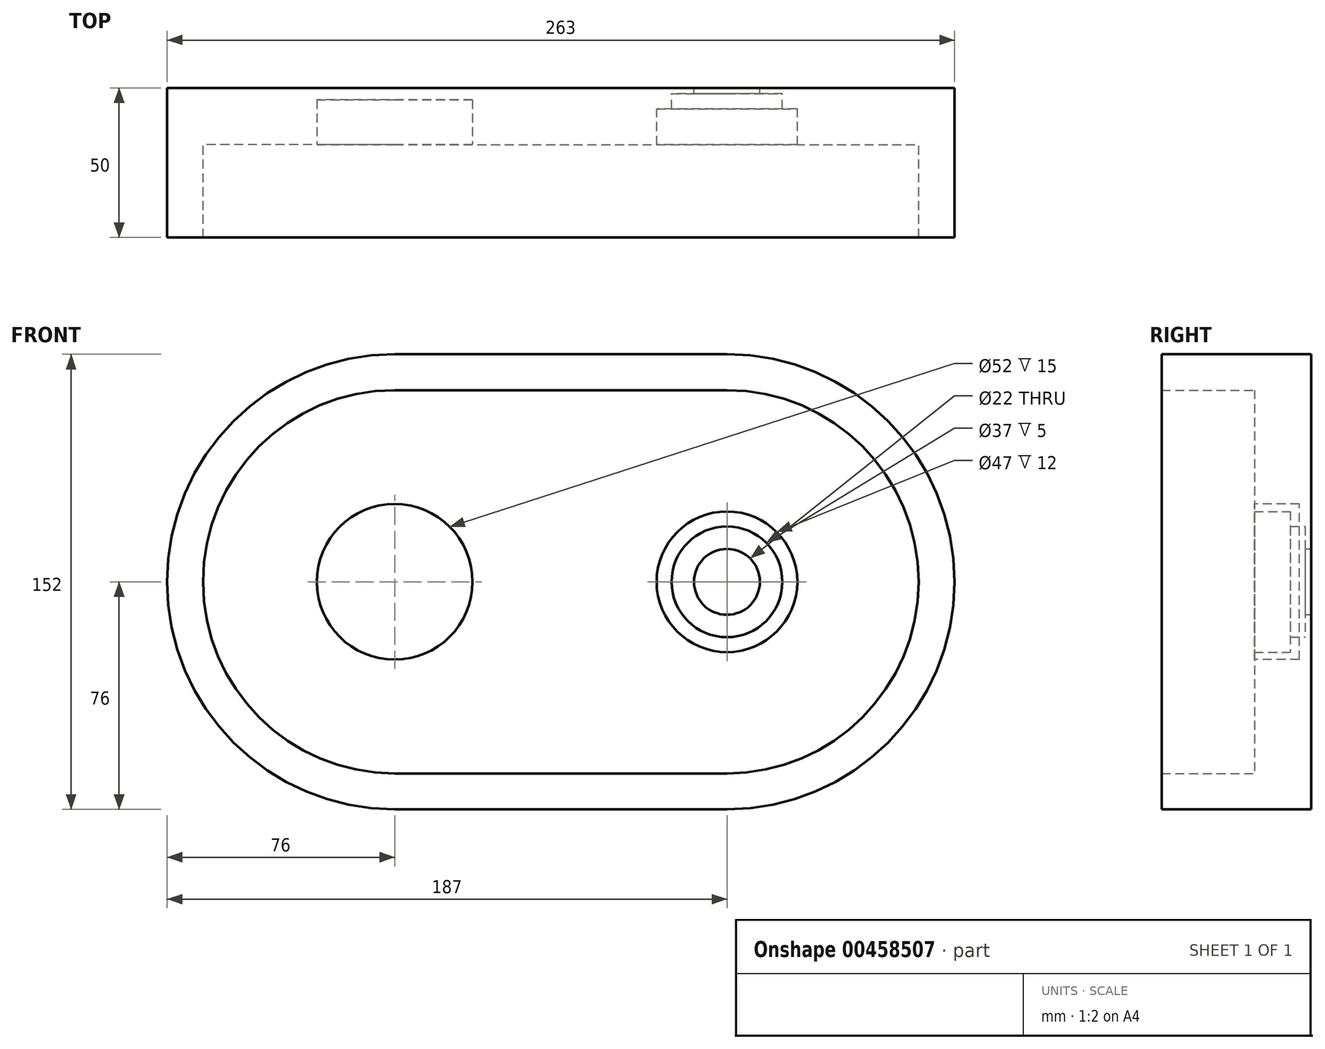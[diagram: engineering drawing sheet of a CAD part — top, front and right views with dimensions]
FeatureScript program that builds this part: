
annotation { "Feature Type Name" : "Feature", "Feature Type Description" : "" }
export const myFeature = defineFeature(function(context is Context, id is Id, definition is map)
    precondition{}
    {
        {
            var Q0;
            Q0=qCreatedBy(makeId("Front.planeOp"),FACE);
            var sketch = newSketch(context, id + "F0", { "sketchPlane" : qUnion([Q0])});
            skArc(sketch, "E0", {"start": v(0, 76) * mm, "mid": v(-76, 0) * mm, "end": v(0, -76) * mm});
            skArc(sketch, "E1", {"start": v(111, -76) * mm, "mid": v(187, 0) * mm, "end": v(111, 76) * mm});
            skLineSegment(sketch, "E2", {"start": v(0, 76) * mm, "end": v(111, 76) * mm});
            skLineSegment(sketch, "E3", {"start": v(111, -76) * mm, "end": v(0, -76) * mm});
            skSolve(sketch);
        }
        {
            var Q0;
            Q0=makeQuery(id+"F0.imprint","IMPRINT",FACE,{"disambiguationData":[TD([[makeQuery(id+"F0.imprint","IMPRINT",EDGE,{"derivedFrom":sQuery(id+"F0.wireOp",EDGE,"E0")}),1.0]])]});
            extrude(context, id + "F1", {"entities" : qUnion([Q0]), "depth" : 50 * mm, "offsetDistance" : 25 * mm});
        }
        {
            var Q0;
            Q0=qCreatedBy(makeId("Front.planeOp"),FACE);
            cPlane(context, id + "F2", {"entities" : qUnion([Q0]), "cplaneType" : CPlaneType.OFFSET, "offset" : 19 * mm, "width" : 150 * mm, "height" : 150 * mm});
        }
        {
            var Q0;
            Q0=qCreatedBy(id+"F2.planeOp",FACE);
            var sketch = newSketch(context, id + "F3", { "sketchPlane" : qUnion([Q0])});
            skArc(sketch, "E4", {"start": v(0, 64) * mm, "mid": v(-64, 0) * mm, "end": v(0, -64) * mm});
            skArc(sketch, "E5", {"start": v(111, -64) * mm, "mid": v(175, 0) * mm, "end": v(111, 64) * mm});
            skLineSegment(sketch, "E6", {"start": v(0, 64) * mm, "end": v(111, 64) * mm});
            skLineSegment(sketch, "E7", {"start": v(0, -64) * mm, "end": v(111, -64) * mm});
            skCircle(sketch, "E8", {"center": v(0, 0) * mm, "radius": 26 * mm});
            skSolve(sketch);
        }
        {
            var Q0;
            Q0 = qSketchRegion(id + "F3", true);
            extrude(context, id + "F4", {"entities" : qUnion([Q0]), "operationType" : NewBodyOperationType.REMOVE, "depth" : 50 * mm, "offsetDistance" : 25 * mm});
        }
        {
            var Q0;
            Q0=makeQuery(id+"F4.boolean.opBoolean","SPLIT",FACE,{"disambiguationData":[TD([makeQuery(id+"F4.opExtrude","SWEPT_FACE",FACE,{"disambiguationData":[OSD([sQuery(id+"F3.wireOp",EDGE,"E8")])]})])],"derivedFrom":makeQuery(id+"F1.opExtrude","CAP_FACE",FACE,{"disambiguationData":[OSD([sQuery(id+"F0.wireOp",EDGE,"E0"),sQuery(id+"F0.wireOp",EDGE,"E1"),sQuery(id+"F0.wireOp",EDGE,"E2"),sQuery(id+"F0.wireOp",EDGE,"E3")])],"isStart":false})});
            extrude(context, id + "F5", {"entities" : qUnion([Q0]), "operationType" : NewBodyOperationType.REMOVE, "oppositeDirection" : true, "depth" : 46 * mm, "offsetDistance" : 25 * mm});
        }
        {
            var Q0;
            Q0=qCreatedBy(makeId("Right.planeOp"),FACE);
            cPlane(context, id + "F6", {"entities" : qUnion([Q0]), "cplaneType" : CPlaneType.OFFSET, "offset" : 111 * mm, "width" : 150 * mm, "height" : 150 * mm});
        }
        {
            var Q0;
            Q0=qCreatedBy(id+"F6.planeOp",FACE);
            var sketch = newSketch(context, id + "F7", { "sketchPlane" : qUnion([Q0])});
            skLineSegment(sketch, "E9", {"start": v(0, 0) * mm, "end": v(0, 11) * mm});
            skLineSegment(sketch, "E10", {"start": v(0, 11) * mm, "end": v(-2, 11) * mm});
            skLineSegment(sketch, "E11", {"start": v(-2, 18.5) * mm, "end": v(-2, 11) * mm});
            skLineSegment(sketch, "E12", {"start": v(0, 0) * mm, "end": v(-49.47, 0) * mm, "construction": true});
            skLineSegment(sketch, "E13", {"start": v(-2, 18.5) * mm, "end": v(-7, 18.5) * mm});
            skLineSegment(sketch, "E14", {"start": v(-7, 18.5) * mm, "end": v(-7, 23.5) * mm});
            skLineSegment(sketch, "E15", {"start": v(-7, 23.5) * mm, "end": v(-19, 23.5) * mm});
            skLineSegment(sketch, "E16", {"start": v(-19, 23.5) * mm, "end": v(-19, 0) * mm});
            skLineSegment(sketch, "E17", {"start": v(-19, 0) * mm, "end": v(0, 0) * mm});
            skSolve(sketch);
        }
        {
            var Q0;
            Q0 = qSketchRegion(id + "F7", true);
            var Q1;
            Q1=makeQuery(id+"F1.opExtrude","SWEPT_FACE",FACE,{"disambiguationData":[OSD([sQuery(id+"F0.wireOp",EDGE,"E1")])]});
            revolve(context, id + "F8", {"operationType" : NewBodyOperationType.REMOVE, "entities" : qUnion([Q0]), "axis" : qUnion([Q1]), "revolveType" : RevolveType.FULL, "oppositeDirection" : true});
        }
    });
